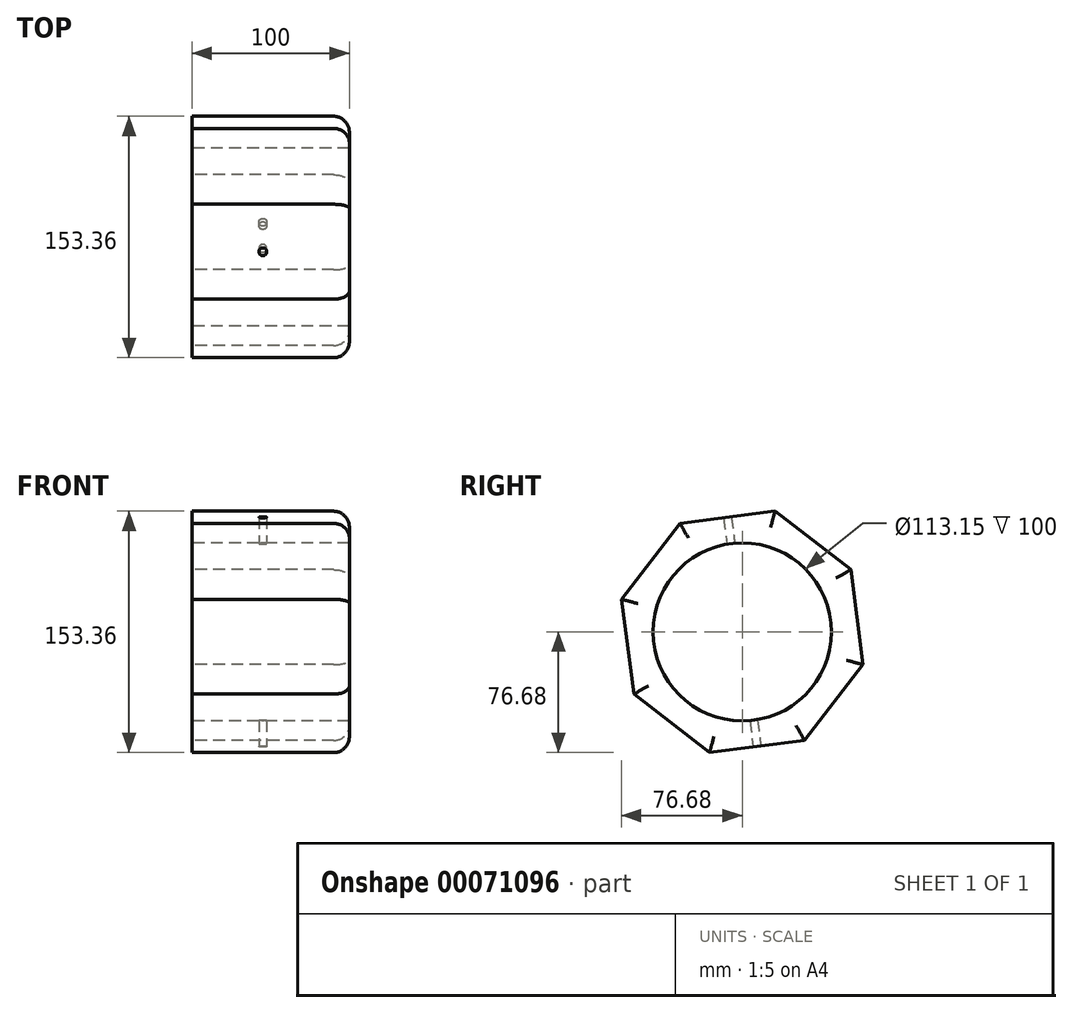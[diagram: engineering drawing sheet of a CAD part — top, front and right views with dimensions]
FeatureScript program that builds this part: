
annotation { "Feature Type Name" : "Feature", "Feature Type Description" : "" }
export const myFeature = defineFeature(function(context is Context, id is Id, definition is map)
    precondition{}
    {
        {
            var Q0;
            Q0=qCreatedBy(makeId("Right.planeOp"),FACE);
            var sketch = newSketch(context, id + "F0", { "sketchPlane" : qUnion([Q0])});
            skCircle(sketch, "E0.cCircle", {"center": v(0, 0) * mm, "radius": 73.4 * mm, "construction": true});
            skLineSegment(sketch, "E0.0", {"start": v(76.68, -20.78) * mm, "end": v(39.53, -68.91) * mm});
            skLineSegment(sketch, "E0.1", {"start": v(39.53, -68.91) * mm, "end": v(-20.78, -76.68) * mm});
            skLineSegment(sketch, "E0.2", {"start": v(-20.78, -76.68) * mm, "end": v(-68.91, -39.53) * mm});
            skLineSegment(sketch, "E0.3", {"start": v(-68.91, -39.53) * mm, "end": v(-76.68, 20.78) * mm});
            skLineSegment(sketch, "E0.4", {"start": v(-76.68, 20.78) * mm, "end": v(-39.53, 68.91) * mm});
            skLineSegment(sketch, "E0.5", {"start": v(-39.53, 68.91) * mm, "end": v(20.78, 76.68) * mm});
            skLineSegment(sketch, "E0.6", {"start": v(20.78, 76.68) * mm, "end": v(68.91, 39.53) * mm});
            skLineSegment(sketch, "E0.7", {"start": v(68.91, 39.53) * mm, "end": v(76.68, -20.78) * mm});
            skPoint(sketch, "E0.0.midPoint", {"position": v(58.1, -44.85) * mm});
            skCircle(sketch, "E1", {"center": v(0, 0) * mm, "radius": 56.57 * mm});
            skSolve(sketch);
        }
        {
            var Q0;
            Q0=makeQuery(id+"F0.imprint","IMPRINT",FACE,{"disambiguationData":[TD([[makeQuery(id+"F0.imprint","IMPRINT",EDGE,{"derivedFrom":sQuery(id+"F0.wireOp",EDGE,"E0.0")}),-1.0]])]});
            extrude(context, id + "F1", {"entities" : qUnion([Q0]), "depth" : 100 * mm});
        }
        {
            var Q0;
            Q0=makeQuery(id+"F1.opExtrude","CAP_EDGE",EDGE,{"disambiguationData":[OSD([sQuery(id+"F0.wireOp",EDGE,"E0.5")])],"isStart":false});
            var Q1;
            Q1=makeQuery(id+"F1.opExtrude","CAP_EDGE",EDGE,{"disambiguationData":[OSD([sQuery(id+"F0.wireOp",EDGE,"E0.4")])],"isStart":false});
            var Q2;
            Q2=makeQuery(id+"F1.opExtrude","CAP_EDGE",EDGE,{"disambiguationData":[OSD([sQuery(id+"F0.wireOp",EDGE,"E0.3")])],"isStart":false});
            var Q3;
            Q3=makeQuery(id+"F1.opExtrude","CAP_EDGE",EDGE,{"disambiguationData":[OSD([sQuery(id+"F0.wireOp",EDGE,"E0.2")])],"isStart":false});
            var Q4;
            Q4=makeQuery(id+"F1.opExtrude","CAP_EDGE",EDGE,{"disambiguationData":[OSD([sQuery(id+"F0.wireOp",EDGE,"E0.1")])],"isStart":false});
            var Q5;
            Q5=makeQuery(id+"F1.opExtrude","CAP_EDGE",EDGE,{"disambiguationData":[OSD([sQuery(id+"F0.wireOp",EDGE,"E0.0")])],"isStart":false});
            var Q6;
            Q6=makeQuery(id+"F1.opExtrude","CAP_EDGE",EDGE,{"disambiguationData":[OSD([sQuery(id+"F0.wireOp",EDGE,"E0.7")])],"isStart":false});
            var Q7;
            Q7=makeQuery(id+"F1.opExtrude","CAP_EDGE",EDGE,{"disambiguationData":[OSD([sQuery(id+"F0.wireOp",EDGE,"E0.6")])],"isStart":false});
            fillet(context, id + "F2", {"entities" : qUnion([Q0, Q1, Q2, Q3, Q4, Q5, Q6, Q7]), "radius" : 10 * mm, "tangentPropagation" : true, "allowEdgeOverflow" : false});
        }
        {
            var Q0;
            Q0=makeQuery(id+"F1.opExtrude","SWEPT_FACE",FACE,{"disambiguationData":[OSD([sQuery(id+"F0.wireOp",EDGE,"E0.1")])]});
            var sketch = newSketch(context, id + "F3", { "sketchPlane" : qUnion([Q0])});
            skPoint(sketch, "E2", {"position": v(45, 0) * mm});
            skLineSegment(sketch, "E3", {"start": v(45, 0) * mm, "end": v(0, 0) * mm});
            skSolve(sketch);
        }
        {
            var Q0;
            Q0=sQuery(id+"F3.wireOp",VERTEX,"E2");
            var Q1;
            Q1=makeQuery(id+"F1.opExtrude","SWEPT_BODY",BODY,{"disambiguationData":[OSD([sQuery(id+"F0.wireOp",EDGE,"E0.0"),sQuery(id+"F0.wireOp",EDGE,"E0.1"),sQuery(id+"F0.wireOp",EDGE,"E0.2"),sQuery(id+"F0.wireOp",EDGE,"E0.3"),sQuery(id+"F0.wireOp",EDGE,"E0.4"),sQuery(id+"F0.wireOp",EDGE,"E0.5"),sQuery(id+"F0.wireOp",EDGE,"E0.6"),sQuery(id+"F0.wireOp",EDGE,"E0.7"),sQuery(id+"F0.wireOp",EDGE,"E1")])]});
            hole(context, id + "F4", {"style" : HoleStyle.SIMPLE, "holeDiameter" : 5 * mm, "endStyle" : HoleEndStyle.THROUGH, "locations" : qUnion([Q0]), "scope" : qUnion([Q1])});
        }
    });
